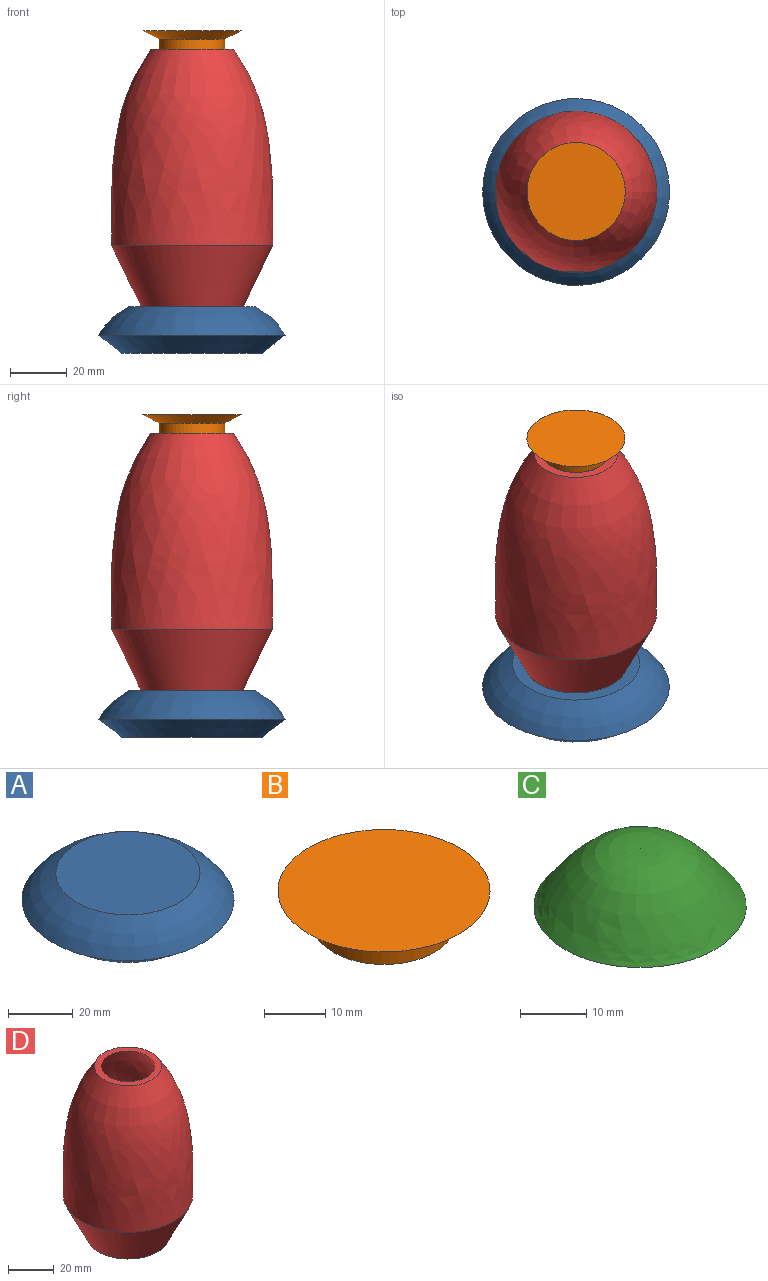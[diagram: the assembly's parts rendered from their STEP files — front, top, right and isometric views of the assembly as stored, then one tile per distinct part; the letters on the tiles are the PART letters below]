
ASSEMBLY  parts=4 mates=3
PART A: 4 faces, bbox 65.7x65.7x16.3 mm
  f0: plane 44.69x44.69mm, normal (0,0,1), area 1568.5mm2, adj f1
  f1: revolved ~65.71x65.71mm, area 2587mm2, adj f0,f2
  f2: cone r=32.86mm half-angle=51.8deg, axis (0,0,1), area 1857.6mm2, adj f1,f3
  f3: plane 49.59x49.59mm, normal (0,0,-1), area 1931.7mm2, adj f2
PART B: 4 faces, bbox 34.5x34.5x6.5 mm
  f0: cylinder r=11.57mm len=23.13mm, axis (0,0,-1), area 266.3mm2, adj f1,f3
  f1: plane 23.13x23.13mm, normal (0,0,-1), area 420.2mm2, adj f0
  f2: plane 34.5x34.5mm, normal (0,0,1), area 935mm2, adj f3
  f3: cone r=17.25mm half-angle=63.4deg, axis (0,0,1), area 575.5mm2, adj f0,f2
PART C: 2 faces, bbox 32x32x10.7 mm
  f0: revolved ~32.05x32.05mm, area 1151.7mm2, adj f1
  f1: plane 32.05x32.05mm, normal (0,0,-1), area 806.7mm2, adj f0
PART D: 7 faces, bbox 56.8x56.8x90.5 mm
  f0: plane 29.3x29.3mm, normal (0,0,1), area 250mm2, adj f1,f4
  f1: revolved ~68.94x56.85mm, area 11340.5mm2, adj f0,f2
  f2: revolved ~56.68x56.68mm, area 3475.5mm2, adj f1,f3
  f3: plane 35.97x35.97mm, normal (0,0,-1), area 1016.1mm2, adj f2
  f4: revolved ~68.39x51.85mm, area 10096.7mm2, adj f0,f5
  f5: revolved ~51.66x51.66mm, area 2883mm2, adj f4,f6
  f6: plane 32.81x32.81mm, normal (0,0,1), area 845.4mm2, adj f5
PLACE A t=(-6.83,7.63,26.21)mm
PLACE B t=(-6.83,7.63,29.09)mm
PLACE C t=(-6.83,7.63,22.58)mm
PLACE D t=(-6.83,7.63,25.66)mm
MATE fastened D.f3 <-> C.f1  axis (0,0,1) through (-6.83,7.63,11.9)mm
MATE fastened B.f0 <-> D.f0  axis (0,0,-1) through (-6.83,7.63,102.37)mm
MATE fastened D.f3 <-> A.f2  axis (0,0,-1) through (-6.83,7.63,11.9)mm
